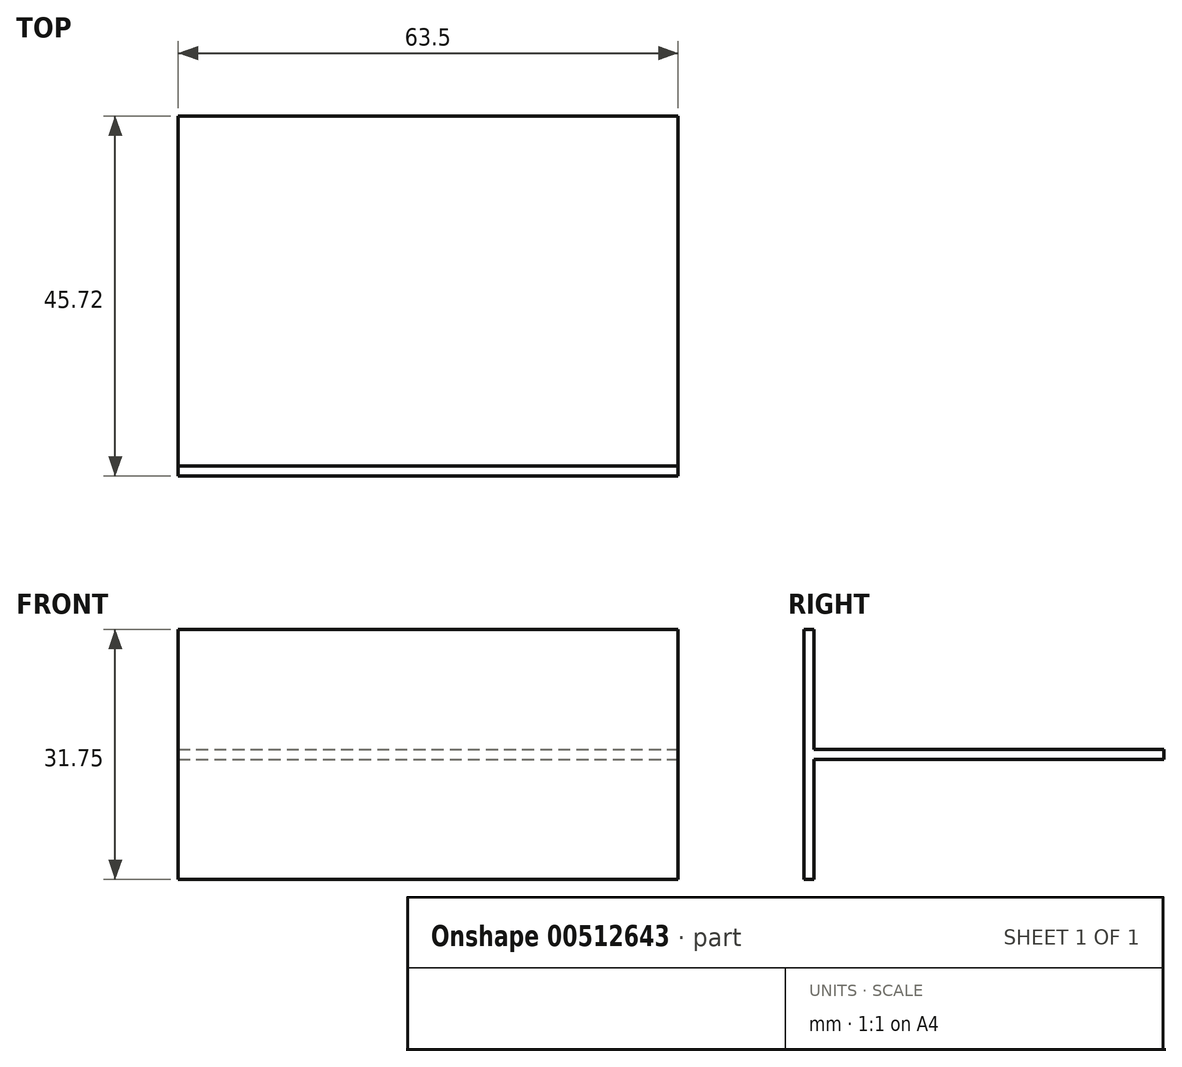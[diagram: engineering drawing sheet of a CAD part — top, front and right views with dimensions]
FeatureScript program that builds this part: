
annotation { "Feature Type Name" : "Feature", "Feature Type Description" : "" }
export const myFeature = defineFeature(function(context is Context, id is Id, definition is map)
    precondition{}
    {
        {
            var Q0;
            Q0=qCreatedBy(makeId("Top.planeOp"),FACE);
            var sketch = newSketch(context, id + "F0", { "sketchPlane" : qUnion([Q0])});
            skLineSegment(sketch, "E0.bottom", {"start": v(0, 0) * mm, "end": v(63.5, 0) * mm});
            skLineSegment(sketch, "E0.top", {"start": v(0, -44.45) * mm, "end": v(63.5, -44.45) * mm});
            skLineSegment(sketch, "E0.left", {"start": v(0, 0) * mm, "end": v(0, -44.45) * mm});
            skLineSegment(sketch, "E0.right", {"start": v(63.5, 0) * mm, "end": v(63.5, -44.45) * mm});
            skSolve(sketch);
        }
        {
            var Q0;
            Q0 = qSketchRegion(id + "F0", true);
            extrude(context, id + "F1", {"entities" : qUnion([Q0]), "depth" : 1.27 * mm});
        }
        {
            var Q0;
            Q0=makeQuery(id+"F1.opExtrude","SWEPT_FACE",FACE,{"disambiguationData":[OSD([sQuery(id+"F0.wireOp",EDGE,"E0.top")])]});
            var sketch = newSketch(context, id + "F2", { "sketchPlane" : qUnion([Q0])});
            skPoint(sketch, "E1.endSnap0", {"position": v(0, 0.64) * mm});
            skLineSegment(sketch, "E2", {"start": v(0, 16.5) * mm, "end": v(0, -15.24) * mm});
            skLineSegment(sketch, "E3", {"start": v(0, 16.51) * mm, "end": v(66.85, 16.5) * mm});
            skLineSegment(sketch, "E4", {"start": v(63.5, 16.51) * mm, "end": v(63.5, -15.24) * mm});
            skLineSegment(sketch, "E5", {"start": v(63.5, -15.24) * mm, "end": v(0, -15.24) * mm});
            skSolve(sketch);
        }
        {
            var Q0;
            Q0 = qSketchRegion(id + "F2", true);
            extrude(context, id + "F3", {"entities" : qUnion([Q0]), "operationType" : NewBodyOperationType.ADD, "depth" : 1.27 * mm});
        }
    });
